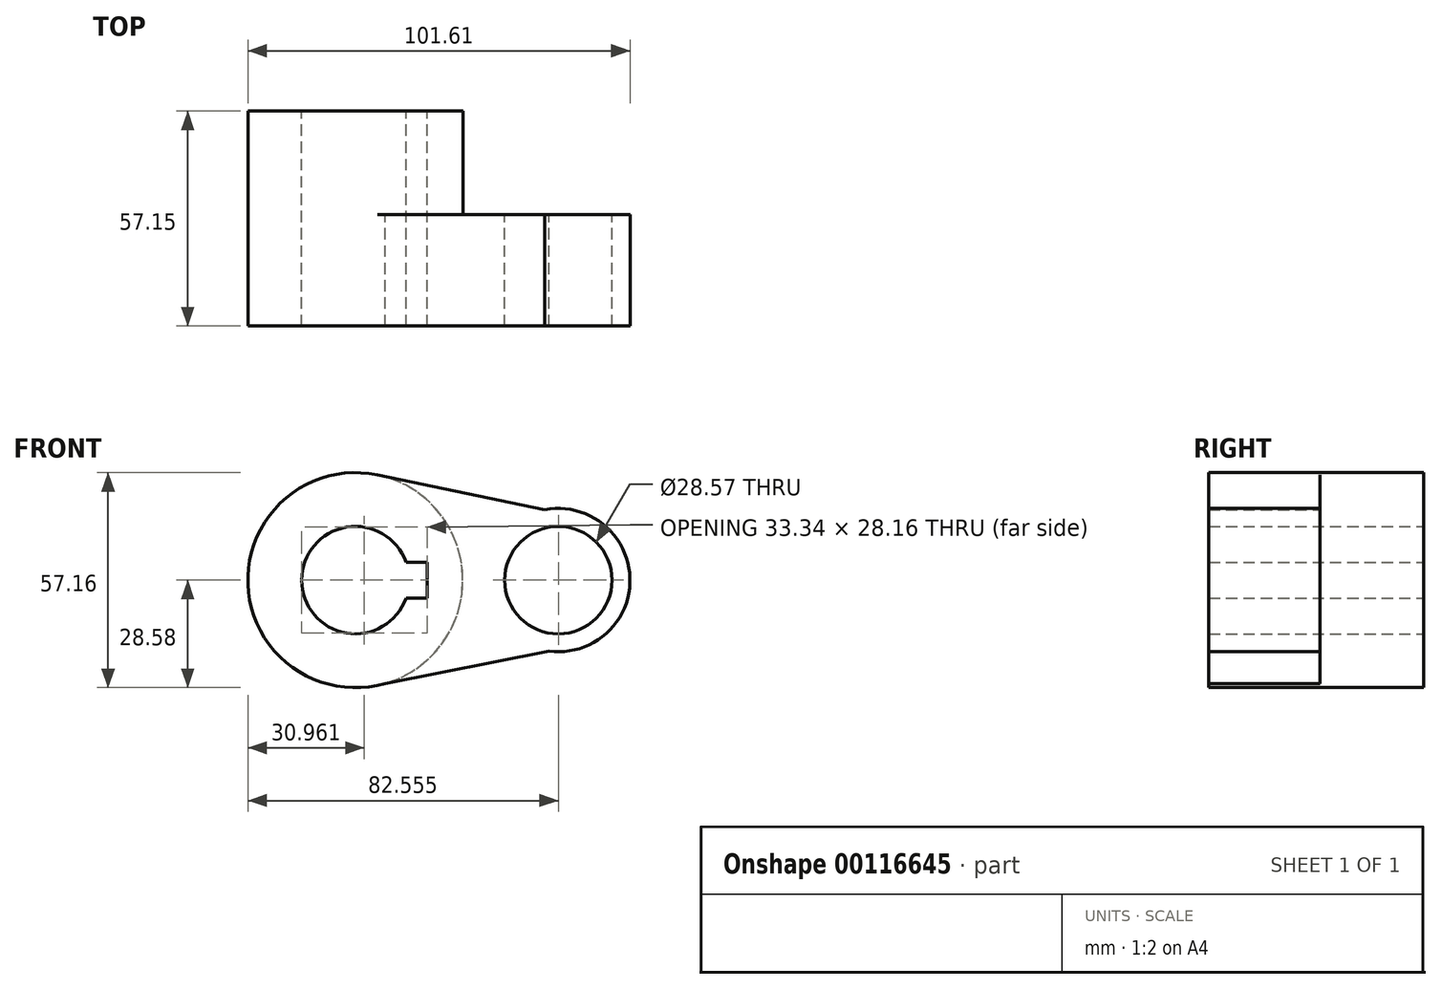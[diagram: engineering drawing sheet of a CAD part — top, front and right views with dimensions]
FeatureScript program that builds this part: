
annotation { "Feature Type Name" : "Feature", "Feature Type Description" : "" }
export const myFeature = defineFeature(function(context is Context, id is Id, definition is map)
    precondition{}
    {
        {
            var Q0;
            Q0=qCreatedBy(makeId("Front.planeOp"),FACE);
            var sketch = newSketch(context, id + "F0", { "sketchPlane" : qUnion([Q0])});
            skCircle(sketch, "E0", {"center": v(0, 0) * mm, "radius": 28.58 * mm});
            skCircle(sketch, "E1", {"center": v(53.98, 0) * mm, "radius": 19.05 * mm});
            skLineSegment(sketch, "E2", {"start": v(5.83, 27.97) * mm, "end": v(50.32, 18.7) * mm});
            skLineSegment(sketch, "E3", {"start": v(7.93, -27.45) * mm, "end": v(51.43, -18.88) * mm});
            skCircle(sketch, "E4", {"center": v(0, 0) * mm, "radius": 14.29 * mm});
            skCircle(sketch, "E5", {"center": v(53.98, 0) * mm, "radius": 14.29 * mm});
            skLineSegment(sketch, "E6.bottom", {"start": v(-19.05, 4.76) * mm, "end": v(19.05, 4.76) * mm});
            skLineSegment(sketch, "E6.top", {"start": v(-19.05, -4.76) * mm, "end": v(19.05, -4.76) * mm});
            skLineSegment(sketch, "E6.left", {"start": v(-19.05, 4.76) * mm, "end": v(-19.05, -4.76) * mm});
            skLineSegment(sketch, "E6.right", {"start": v(19.05, 4.76) * mm, "end": v(19.05, -4.76) * mm});
            skSolve(sketch);
        }
        {
            var Q0;
            {var subQ0=sQuery(id+"F0.wireOp",EDGE,"E2");Q0=makeQuery(id+"F0.imprint","IMPRINT",FACE,{"disambiguationData":[TD([[makeQuery(id+"F0.imprint","IMPRINT",EDGE,{"derivedFrom":subQ0}),-1.0]])]});}
            var Q1;
            Q1=makeQuery(id+"F0.imprint","IMPRINT",FACE,{"disambiguationData":[TD([[makeQuery(id+"F0.imprint","IMPRINT",EDGE,{"derivedFrom":sQuery(id+"F0.wireOp",EDGE,"E5")}),-1.0]])]});
            var Q2;
            {var subQ11=sQuery(id+"F0.wireOp",EDGE,"E6.left");Q2=makeQuery(id+"F0.imprint","IMPRINT",FACE,{"disambiguationData":[TD([[makeQuery(id+"F0.imprint","IMPRINT",EDGE,{"derivedFrom":subQ11}),-1.0]])]});}
            var Q3;
            {var subQ5=sQuery(id+"F0.wireOp",EDGE,"E6.left");Q3=makeQuery(id+"F0.imprint","IMPRINT",FACE,{"disambiguationData":[TD([[makeQuery(id+"F0.imprint","IMPRINT",EDGE,{"derivedFrom":subQ5}),1.0]])]});}
            extrude(context, id + "F1", {"entities" : qUnion([Q0, Q1, Q2, Q3]), "depth" : 29.6 * mm});
        }
        {
            var Q0;
            {var subQ11=sQuery(id+"F0.wireOp",EDGE,"E6.left");Q0=makeQuery(id+"F0.imprint","IMPRINT",FACE,{"disambiguationData":[TD([[makeQuery(id+"F0.imprint","IMPRINT",EDGE,{"derivedFrom":subQ11}),-1.0]])]});}
            var Q1;
            {var subQ5=sQuery(id+"F0.wireOp",EDGE,"E6.left");Q1=makeQuery(id+"F0.imprint","IMPRINT",FACE,{"disambiguationData":[TD([[makeQuery(id+"F0.imprint","IMPRINT",EDGE,{"derivedFrom":subQ5}),1.0]])]});}
            extrude(context, id + "F2", {"entities" : qUnion([Q0, Q1]), "operationType" : NewBodyOperationType.ADD, "oppositeDirection" : true, "depth" : 27.55 * mm});
        }
    });
